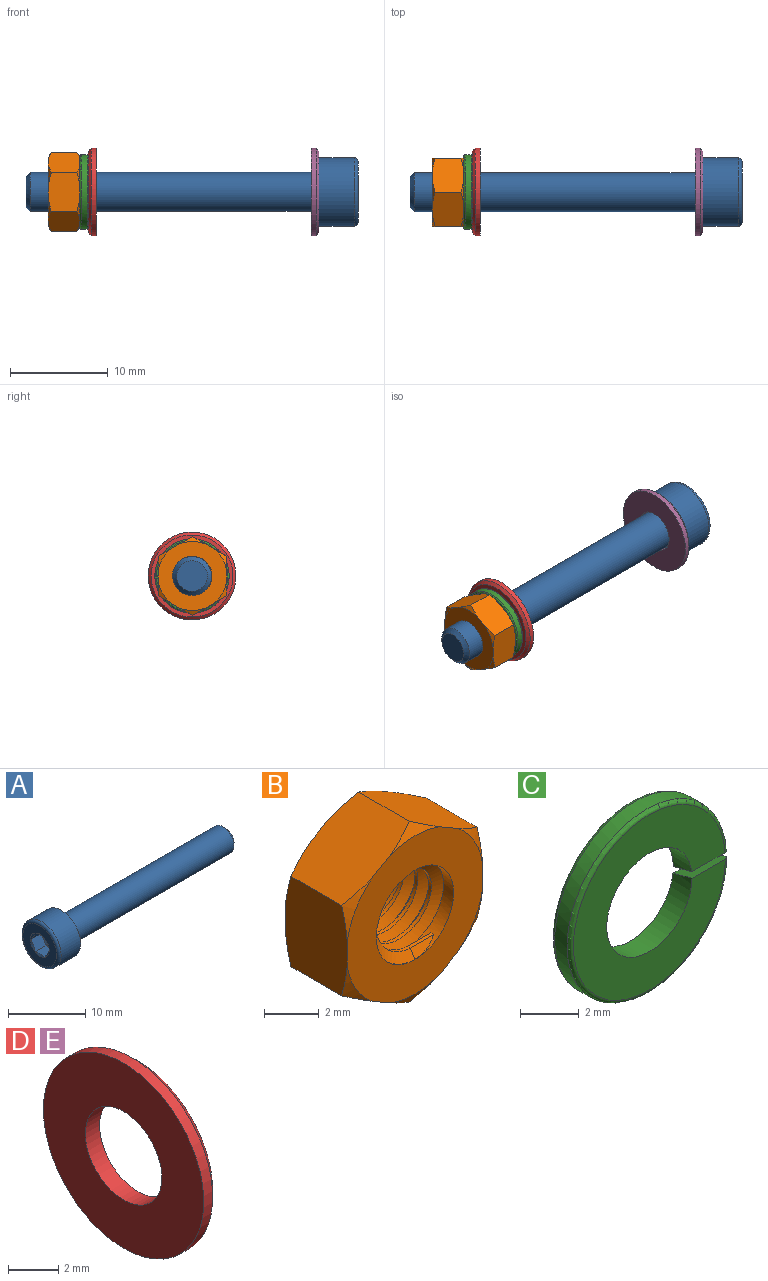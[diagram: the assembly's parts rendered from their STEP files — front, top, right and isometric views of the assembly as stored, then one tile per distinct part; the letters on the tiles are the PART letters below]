
ASSEMBLY  parts=5 mates=4
PART A: 24 faces, bbox 34x7.6x7.6 mm
  f0: plane 1.3x0.75mm, normal (-1,0,0), area 0.1mm2, adj f16,f17,f23
  f1: plane 1.5x0.43mm, normal (-1,0,0), area 0.1mm2, adj f17,f18,f23
  f2: plane 1.3x0.75mm, normal (-1,0,0), area 0.1mm2, adj f18,f19,f23
  f3: plane 1.3x0.75mm, normal (-1,0,0), area 0.1mm2, adj f19,f20,f23
  f4: plane 1.5x0.43mm, normal (-1,0,0), area 0.1mm2, adj f20,f21,f23
  f5: cone r=1.74mm half-angle=60deg, axis (-1,0,0), area 2mm2, adj f15,f16,f17,f18,f19,f20,f21
  f6: cone r=2.01mm half-angle=20.6deg, axis (-1,0,0), area 5.6mm2, adj f7,f11
  f7: torus R=2.2mm, axis (1,0,0), area 0.9mm2, adj f6,f10
  f8: plane 3.14x3.14mm, normal (1,0,0), area 7.7mm2, adj f9
  f9: cone r=2mm half-angle=45deg, axis (-1,0,0), area 6.8mm2, adj f8,f10
  f10: cylinder r=2mm len=28.97mm, axis (1,0,0), area 364.1mm2, adj f7,f9
  f11: torus R=2.35mm, axis (1,0,0), area 3.4mm2, adj f6,f13
  f12: cylinder r=3.5mm len=7mm, axis (1,0,0), area 79.2mm2, adj f13,f14
  f13: plane 7x7mm, normal (1,0,0), area 21.1mm2, adj f11,f12
  f14: torus R=3.1mm, axis (1,0,0), area 13.2mm2, adj f12,f15
  f15: plane 6.2x6.2mm, normal (-1,0,0), area 20.7mm2, adj f5,f14
  f16: plane 2x1.74mm, normal (0,0,-1), area 3.3mm2, adj f0,f5,f17,f21,f22
  f17: plane 2x1.5mm, normal (0,0.87,-0.5), area 3.3mm2, adj f0,f1,f5,f16,f18
  f18: plane 2x1.5mm, normal (0,0.87,0.5), area 3.3mm2, adj f1,f2,f5,f17,f19
  f19: plane 2x1.74mm, normal (0,0,1), area 3.3mm2, adj f2,f3,f5,f18,f20
  f20: plane 2x1.5mm, normal (0,-0.87,0.5), area 3.3mm2, adj f3,f4,f5,f19,f21
  f21: plane 2x1.5mm, normal (0,-0.87,-0.5), area 3.3mm2, adj f4,f5,f16,f20,f22
  f22: plane 1.3x0.75mm, normal (-1,0,0), area 0.1mm2, adj f16,f21,f23
  f23: cone r=1.5mm half-angle=60deg, axis (-1,0,0), area 8.2mm2, adj f0,f1,f2,f3,f4,f22
PART B: 28 faces, bbox 8.2x3.5x8.3 mm
  f0: cone r=3.54mm half-angle=60deg, axis (0,-1,0), area 0.8mm2, adj f11,f22,f23
  f1: cone r=3.54mm half-angle=60deg, axis (0,-1,0), area 0.8mm2, adj f11,f23,f24
  f2: cone r=3.54mm half-angle=60deg, axis (0,-1,0), area 0.8mm2, adj f11,f24,f25
  f3: cone r=3.54mm half-angle=60deg, axis (0,-1,0), area 0.8mm2, adj f11,f25,f26
  f4: cone r=3.54mm half-angle=60deg, axis (0,-1,0), area 0.8mm2, adj f11,f22,f27
  f5: cone r=4.04mm half-angle=60deg, axis (0,1,0), area 0.8mm2, adj f10,f22,f23
  f6: cone r=4.04mm half-angle=60deg, axis (0,1,0), area 0.8mm2, adj f10,f23,f24
  f7: cone r=4.04mm half-angle=60deg, axis (0,1,0), area 0.8mm2, adj f10,f24,f25
  f8: cone r=4.04mm half-angle=60deg, axis (0,1,0), area 0.8mm2, adj f10,f25,f26
  f9: cone r=4.04mm half-angle=60deg, axis (0,1,0), area 0.8mm2, adj f10,f26,f27
  f10: plane 7.08x7mm, normal (0,-1,0), area 26.7mm2, adj f5,f6,f7,f8,f9,f12,f21,f22
  f11: plane 7.08x7mm, normal (0,1,0), area 26.7mm2, adj f0,f1,f2,f3,f4,f12,f20,f22
  f12: cylinder r=2mm len=4mm, axis (0,1,0), area 11.1mm2, adj f10,f11,f13,f15,f16,f17,f18,f19
  f13: plane 0.62x0.38mm, normal (0.35,0,-0.94), area 0.2mm2, adj f12,f14,f15,f16
  f14: cylinder r=1.6mm len=3.2mm, axis (0,1,0), area 5.7mm2, adj f13,f15,f16,f17
  f15: bspline ~4.62x4mm, area 19.3mm2, adj f12,f13,f14,f18
  f16: bspline ~4.62x4mm, area 19.3mm2, adj f12,f13,f14,f19
  f17: plane 1.2x0.15mm, normal (0,0,1), area 0.2mm2, adj f12,f14,f18,f19
  f18: plane 1.31x0.51mm, normal (0,0.87,0.5), area 0.4mm2, adj f12,f15,f17
  f19: plane 1.31x0.51mm, normal (0,-0.87,0.5), area 0.4mm2, adj f12,f16,f17
  f20: cone r=3.54mm half-angle=60deg, axis (0,-1,0), area 0.8mm2, adj f11,f26,f27
  f21: cone r=4.04mm half-angle=60deg, axis (0,1,0), area 0.8mm2, adj f10,f22,f27
  f22: plane 3.68x3.38mm, normal (-0.5,0,0.87), area 12.2mm2, adj f0,f4,f5,f10,f11,f21,f23,f27
  f23: plane 3.68x3.38mm, normal (0.5,0,0.87), area 12.2mm2, adj f0,f1,f5,f6,f10,f11,f22,f24
  f24: plane 4.23x3.38mm, normal (1,0,0), area 12.2mm2, adj f1,f2,f6,f7,f10,f11,f23,f25
  f25: plane 3.68x3.38mm, normal (0.5,0,-0.87), area 12.2mm2, adj f2,f3,f7,f8,f10,f11,f24,f26
  f26: plane 3.68x3.38mm, normal (-0.5,0,-0.87), area 12.2mm2, adj f3,f8,f9,f10,f11,f20,f25,f27
  f27: plane 4.23x3.38mm, normal (-1,0,0), area 12.2mm2, adj f4,f9,f10,f11,f20,f21,f22,f26
PART C: 8 faces, bbox 8.2x0.9x8.2 mm
  f0: cylinder r=2.05mm len=4.1mm, axis (0,1,0), area 11.3mm2, adj f2,f3,f4,f5
  f1: cylinder r=3.8mm len=7.6mm, axis (0,1,0), area 14.2mm2, adj f4,f5,f6,f7
  f2: plane 7.3x7.3mm, normal (0,-1,0), area 28.2mm2, adj f0,f4,f5,f6
  f3: plane 7.3x7.3mm, normal (0,1,0), area 28.2mm2, adj f0,f4,f5,f7
  f4: plane 1.78x0.92mm, normal (0,-0.26,-0.97), area 1.6mm2, adj f0,f1,f2,f3,f6,f7
  f5: plane 1.78x0.92mm, normal (0,0.26,0.97), area 1.6mm2, adj f0,f1,f2,f3,f6,f7
  f6: torus R=3.65mm, axis (0,1,0), area 5.5mm2, adj f1,f2,f4,f5
  f7: torus R=3.65mm, axis (0,1,0), area 5.5mm2, adj f1,f3,f4,f5
PART D: 5 faces, bbox 0.8x9x9 mm
  f0: plane 9x9mm, normal (-1,0,0), area 49.1mm2, adj f1,f4
  f1: cylinder r=2.15mm len=4.3mm, axis (1,0,0), area 10.8mm2, adj f0,f2
  f2: plane 8.4x8.4mm, normal (1,0,0), area 40.9mm2, adj f1,f3
  f3: cone r=4.2mm half-angle=45deg, axis (-1,0,0), area 11.6mm2, adj f2,f4
  f4: cylinder r=4.5mm len=9mm, axis (1,0,0), area 14.1mm2, adj f0,f3
PART E: same geometry as D
PLACE A rot(axis=(0,1,0),180deg) t=(0.8,0,0)mm
PLACE B rot(axis=(0,0,1),90deg) t=(-26.9,-0.04,0)mm
PLACE C rot(axis=(0,0,1),90deg) t=(-23.7,0,0)mm
PLACE D rot(axis=(0,1,0),180deg) t=(-22,0,0)mm
PLACE E at identity fixed
MATE fastened D.f1 <-> E.f1  axis (1,0,0) through (-22,0,0)mm
MATE fastened A.f5 <-> E.f1  axis (-1,0,0) through (0.8,0,0)mm
MATE fastened B.f0 <-> C.f3  axis (1,0,0) through (-23.7,-0.04,0)mm
MATE fastened C.f0 <-> D.f1  axis (1,0,0) through (-22.8,0,0)mm
